# Revit family: Basin-Wall-Caroma Teo 410
name_source: partatom
category: Plumbing Fixtures
revit_build: Autodesk Revit MEP 2014 (Build: 20140709_2115(x64)
units: mm (PartAtom-declared; Revit-internal decimal feet)

## types (1)
- This family uses a type catalogue
    1TapHoles = No
    Assembly Code = D2010310
    CW Connection = No
    Default Elevation = 865 mm
    HW Connection = No
    Height = 145 mm
    Length = 410 mm
    Manufacturer = GWA Bathrooms & Kitchens
    Material_ANZRS = Porcelain-White-Caroma
    ModifiedIssue_ANZRS = 20151014.54 $
    TapHole1 = 100 mm  [stored 0.328084 ft]
    Type Comments = Caroma Teo 410 Wall Basin
    URL = http://www.specify.caroma.com.au
    Vent Connection = No
    WFU = 1
    Waste = Metal-Chrome-Caroma
    Waste Connection = Yes
    WasteOutlet_ANZRS = 0
    Width = 410 mm

note: [stored X ft] marks values corroborated as IEEE doubles in the binary element streams (Revit-internal decimal feet)

## geometry (parser evidence)
native form markers: Blend x8, Sweep x2
no freeform markers — native parametric forms only
